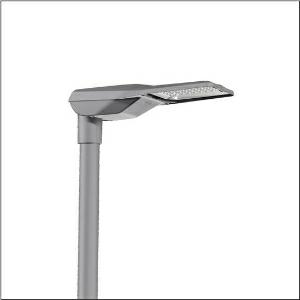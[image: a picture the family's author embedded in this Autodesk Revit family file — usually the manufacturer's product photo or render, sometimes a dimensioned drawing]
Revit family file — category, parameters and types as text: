
# Revit family: streetlight_sl_21_iq_mini___st1_0a_5xe2d41d08jb_acb7
name_source: partatom
category: Lighting Fixtures
units: mm (PartAtom-declared; Revit-internal decimal feet)

## family parameters
Cut with Voids When Loaded = No
Host = Face
Light Source = No
Part Type = Normal
Room Calculation Point = No
Round Connector Dimension = Use Diameter
Shared = No

## types (1)
- --- (1 x LED, 11290 lm, 71.6 W, 4000K)
    Apparent Load = 72 VA
    CIE Flux Codes = 40 73 97 100 100
    Color Rendering = 70
    Color Temperature = 4000K
    Default Elevation = 1800 mm
    Description = Streetlight SL 21 mini, mast luminaire, primary light control with lens, of PMMA, primary optical cover: cover, of toughened safety glass, transparent, light distribution: ST1.0a, light emission: direct distribution, primary light characteristic: asymmetric, installation type: post-top, side-entry, LED, High Power LED, rated luminous flux: 11.290lm, luminous efficacy: 158lm/W, light colour: 740, colour temperature: 4000K, control gear: ECG iQ, control: Auto-Match, Temp-Guard, Lumen-Switch, Night-Set, Smart-Wire, Light-Fading, Desk-Remote (wireless, voltage-free reading and setting of iQ features in the workshop via application-optimized NFC function/RFID function), optimised constant luminous flux control (CLO 2.0), mains connection: 220..240V, AC, 50/60Hz, start of lifetime: 72W, end of lifetime: 75W, reduction: 33W, luminaire housing, of diecast aluminium, powder-coated, Siteco® metallic grey (DB 702S), corrosivity category C5 according to DIN EN ISO 12944, length: 628mm, width: 235mm, height: 110mm, spigot size: 60/76mm (post-top) and 42/60/76mm (side-entry), mast flange for spigot size: 42mm: 5XC10008XM4, 60mm: 5XC10008XM2, 76/60mm: 5XC10108XM1, protection rating (complete): IP66, insulation class (complete): insulation class II (safety insulation), certification: CE, ENEC, VDE, impact resistance: IK09, permissible operating ambient temperature for outdoor applications: -40..+50°C, standard-compliant lighting for roads and squares, packaging unit: 1 piece

Light Distribution: ST1.0a
    Height = 110 mm
    Lamp = 1 x LED
    Lamp Light Flux = 11290 lm
    Lamp Power = 71.6 W
    Lamp count = 1
    Length = 625 mm
    Luminous efficacy = 158 lm/W
    Manufacturer = Siteco
    ModVariant = No
    Model = 5XE2D41D08JB
    Number of Poles = 1
    OnlyDefault = Yes
    Power Factor = 1
    Product Name = Streetlight SL 21 iQ mini | ST1.0a
    Product group = mast luminaire | pylon top
    ProductGroupID = 6100
    Protection Class = Protection class II
    Protection Degree = IP 66
    RLX_Detail_Level = 1
    RlxData = <blob elided: 92917 chars, md5=d5e00586>
    Socket = socket
    Standby Power = 0 W
    System Light Flux = 11290 lm
    System Power = 72 W
    Type Comments = factory setting: luminous flux: 100 % | dim-lin: 254 | 746 mA
    Type Image = l_1003519.jpg
    URL = http://relux.com
    VarID = @adj_083213
    Voltage = 0 V
    Weight = 0.00 kg
    Width = 234 mm

## geometry (parser evidence)
native form markers: Blend x4, Sweep x11
no freeform markers — native parametric forms only
